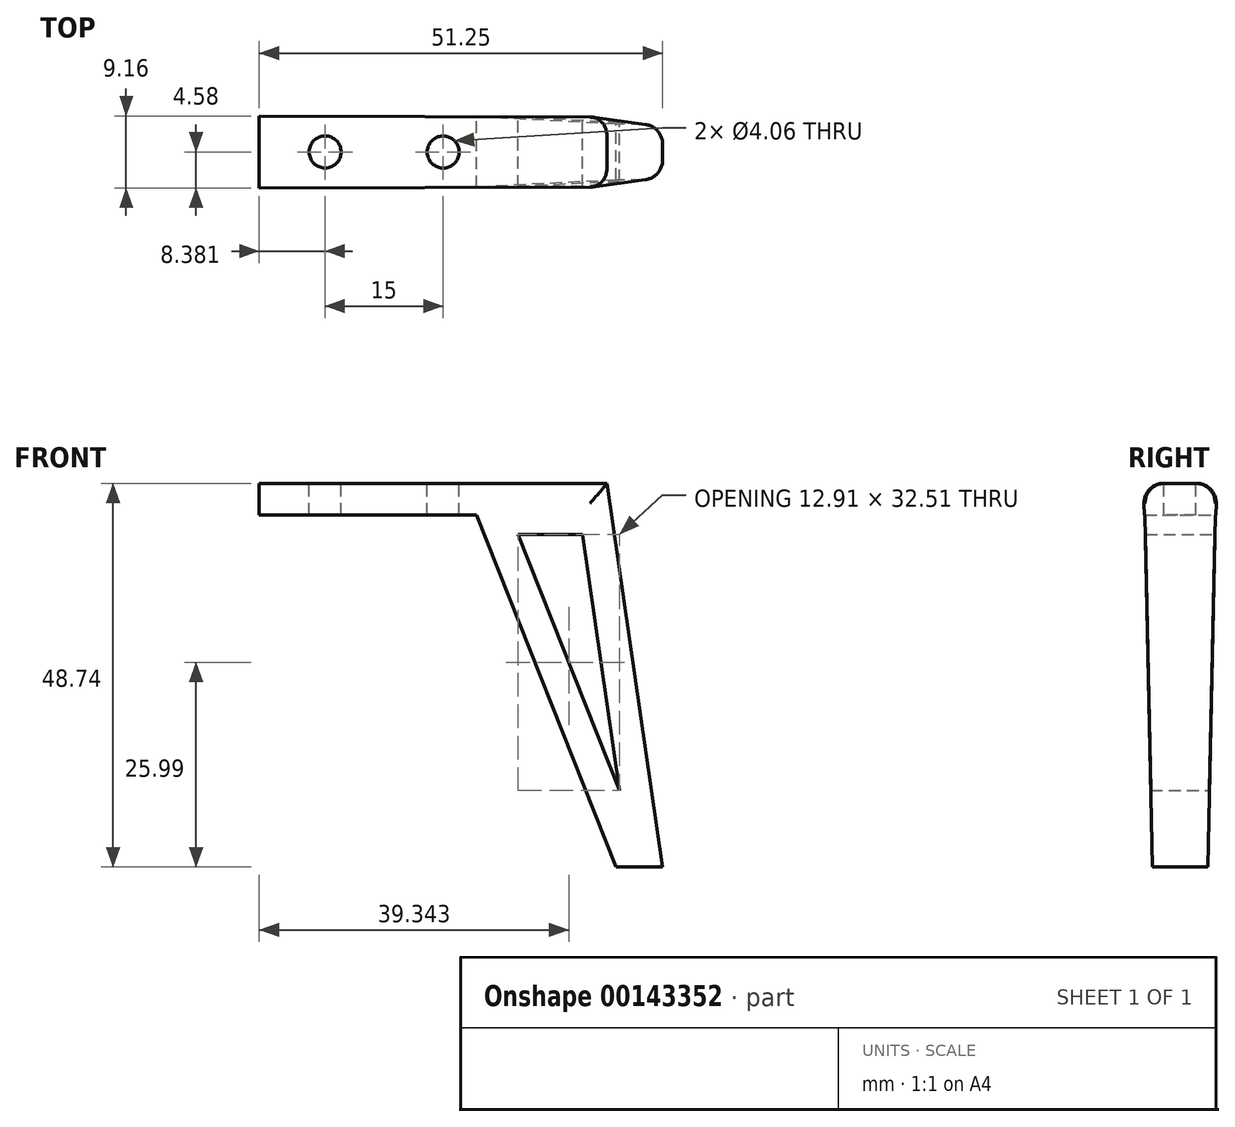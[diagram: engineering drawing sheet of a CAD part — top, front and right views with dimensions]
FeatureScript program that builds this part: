
annotation { "Feature Type Name" : "Feature", "Feature Type Description" : "" }
export const myFeature = defineFeature(function(context is Context, id is Id, definition is map)
    precondition{}
    {
        {
            var Q0;
            Q0=qCreatedBy(makeId("Front.planeOp"),FACE);
            var sketch = newSketch(context, id + "F0", { "sketchPlane" : qUnion([Q0])});
            skLineSegment(sketch, "E0.bottom", {"start": v(-26.8, -2) * mm, "end": v(0.8, -2) * mm});
            skLineSegment(sketch, "E0.top", {"start": v(-26.8, 2) * mm, "end": v(17.39, 2) * mm});
            skLineSegment(sketch, "E0.left", {"start": v(-26.8, -2) * mm, "end": v(-26.8, 2) * mm});
            skPoint(sketch, "E0.middle", {"position": v(0, 0) * mm});
            skLineSegment(sketch, "E1", {"start": v(0, 0) * mm, "end": v(18.56, -46.74) * mm});
            skLineSegment(sketch, "E2", {"start": v(18.56, -46.74) * mm, "end": v(24.45, -46.74) * mm});
            skLineSegment(sketch, "E3", {"start": v(17.39, 2) * mm, "end": v(24.45, -46.74) * mm});
            skPoint(sketch, "E4.orphan", {"position": v(26.8, 2) * mm});
            skPoint(sketch, "E5.orphan", {"position": v(26.8, -2) * mm});
            skLineSegment(sketch, "E6.0", {"start": v(6.09, -4.5) * mm, "end": v(19, -37) * mm});
            skLineSegment(sketch, "E7.0", {"start": v(14.29, -4.5) * mm, "end": v(19, -37) * mm});
            skLineSegment(sketch, "E8", {"start": v(6.09, -4.5) * mm, "end": v(14.29, -4.5) * mm});
            skSolve(sketch);
        }
        {
            var Q0;
            Q0 = qSketchRegion(id + "F0", true);
            extrude(context, id + "F1", {"entities" : qUnion([Q0]), "depth" : 11.5 * mm, "hasSecondDirection" : true, "secondDirectionOppositeDirection" : true, "secondDirectionDepth" : 7.25 * mm});
        }
        {
            var Q0;
            Q0=makeQuery(id+"F1.opExtrude","SWEPT_FACE",FACE,{"disambiguationData":[OSD([sQuery(id+"F0.wireOp",EDGE,"E3")])]});
            cPlane(context, id + "F2", {"entities" : qUnion([Q0]), "cplaneType" : CPlaneType.OFFSET, "offset" : 1.5 * mm, "width" : 150 * mm, "height" : 150 * mm});
        }
        {
            var Q0;
            Q0=qCreatedBy(id+"F2.planeOp",FACE);
            var sketch = newSketch(context, id + "F3", { "sketchPlane" : qUnion([Q0])});
            skLineSegment(sketch, "E9", {"start": v(-17.18, -51.7) * mm, "end": v(-3.49, -51.82) * mm});
            skLineSegment(sketch, "E10.MirrorCS", {"start": v(17.18, -51.7) * mm, "end": v(3.49, -51.82) * mm});
            skLineSegment(sketch, "E11", {"start": v(-3.49, -51.82) * mm, "end": v(-4.72, 10.55) * mm});
            skLineSegment(sketch, "E12", {"start": v(-4.72, 10.55) * mm, "end": v(-18.6, 10.28) * mm});
            skLineSegment(sketch, "E13", {"start": v(-18.6, 10.28) * mm, "end": v(-17.18, -51.7) * mm});
            skLineSegment(sketch, "E14.MirrorCS", {"start": v(3.49, -51.82) * mm, "end": v(4.72, 10.55) * mm});
            skLineSegment(sketch, "E15.MirrorCS", {"start": v(4.72, 10.55) * mm, "end": v(18.6, 10.28) * mm});
            skLineSegment(sketch, "E16.MirrorCS", {"start": v(18.6, 10.28) * mm, "end": v(17.18, -51.7) * mm});
            skSolve(sketch);
        }
        {
            var Q0;
            Q0=makeQuery(id+"F3.imprint","IMPRINT",FACE,{"disambiguationData":[TD([[makeQuery(id+"F3.imprint","IMPRINT",EDGE,{"derivedFrom":sQuery(id+"F3.wireOp",EDGE,"TnA0PpF5-dN3h-Jc00-I28Z-ERWVzqy0urNH")}),1.0]])]});
            var Q1;
            Q1=makeQuery(id+"F3.imprint","IMPRINT",FACE,{"disambiguationData":[TD([[makeQuery(id+"F3.imprint","IMPRINT",EDGE,{"derivedFrom":sQuery(id+"F3.wireOp",EDGE,"81dc0e61-a533-4fef-84a6-d9a5de71d5ed0.MirrorCS")}),-1.0]])]});
            var Q2;
            Q2=makeQuery(id+"F3.imprint","IMPRINT",FACE,{"disambiguationData":[TD([[makeQuery(id+"F3.imprint","IMPRINT",EDGE,{"derivedFrom":sQuery(id+"F3.wireOp",EDGE,"E9")}),1.0]])]});
            var Q3;
            Q3=makeQuery(id+"F3.imprint","IMPRINT",FACE,{"disambiguationData":[TD([[makeQuery(id+"F3.imprint","IMPRINT",EDGE,{"derivedFrom":sQuery(id+"F3.wireOp",EDGE,"E10.MirrorCS")}),-1.0]])]});
            extrude(context, id + "F4", {"entities" : qUnion([Q0, Q1, Q2, Q3]), "operationType" : NewBodyOperationType.REMOVE, "oppositeDirection" : true, "depth" : 57.75 * mm});
        }
        {
            var Q0;
            Q0=makeQuery(id+"F1.opExtrude","SWEPT_FACE",FACE,{"disambiguationData":[OSD([sQuery(id+"F0.wireOp",EDGE,"E0.top")])]});
            var sketch = newSketch(context, id + "F5", { "sketchPlane" : qUnion([Q0])});
            skCircle(sketch, "E17", {"center": v(-3.42, 0) * mm, "radius": 2.03 * mm});
            skCircle(sketch, "E18", {"center": v(-18.42, 0) * mm, "radius": 2.03 * mm});
            skSolve(sketch);
        }
        {
            var Q0;
            Q0=makeQuery(id+"F5.imprint","IMPRINT",FACE,{"disambiguationData":[TD([[makeQuery(id+"F5.imprint","IMPRINT",EDGE,{"derivedFrom":sQuery(id+"F5.wireOp",EDGE,"E17")}),1.0]])]});
            var Q1;
            Q1=makeQuery(id+"F5.imprint","IMPRINT",FACE,{"disambiguationData":[TD([[makeQuery(id+"F5.imprint","IMPRINT",EDGE,{"derivedFrom":sQuery(id+"F5.wireOp",EDGE,"E18")}),1.0]])]});
            extrude(context, id + "F6", {"entities" : qUnion([Q0, Q1]), "operationType" : NewBodyOperationType.REMOVE, "oppositeDirection" : true, "depth" : 25 * mm});
        }
        {
            var Q0;
            Q0=makeQuery(id+"F4.boolean.opBoolean","INTERSECT",EDGE,{"derivedFrom":[makeQuery(id+"F1.opExtrude","SWEPT_FACE",FACE,{"disambiguationData":[OSD([sQuery(id+"F0.wireOp",EDGE,"E0.top")])]}),makeQuery(id+"F4.opExtrude","SWEPT_FACE",FACE,{"disambiguationData":[OSD([sQuery(id+"F3.wireOp",EDGE,"E11")])]})]});
            var Q1;
            Q1=makeQuery(id+"F4.boolean.opBoolean","INTERSECT",EDGE,{"derivedFrom":[makeQuery(id+"F1.opExtrude","SWEPT_FACE",FACE,{"disambiguationData":[OSD([sQuery(id+"F0.wireOp",EDGE,"E0.top")])]}),makeQuery(id+"F4.opExtrude","SWEPT_FACE",FACE,{"disambiguationData":[OSD([sQuery(id+"F3.wireOp",EDGE,"E14.MirrorCS")])]})]});
            var Q2;
            Q2=makeQuery(id+"F4.boolean.opBoolean","INTERSECT",EDGE,{"derivedFrom":[makeQuery(id+"F1.opExtrude","SWEPT_FACE",FACE,{"disambiguationData":[OSD([sQuery(id+"F0.wireOp",EDGE,"E3")])]}),makeQuery(id+"F4.opExtrude","SWEPT_FACE",FACE,{"disambiguationData":[OSD([sQuery(id+"F3.wireOp",EDGE,"E14.MirrorCS")])]})]});
            var Q3;
            Q3=makeQuery(id+"F4.boolean.opBoolean","INTERSECT",EDGE,{"derivedFrom":[makeQuery(id+"F1.opExtrude","SWEPT_FACE",FACE,{"disambiguationData":[OSD([sQuery(id+"F0.wireOp",EDGE,"E3")])]}),makeQuery(id+"F4.opExtrude","SWEPT_FACE",FACE,{"disambiguationData":[OSD([sQuery(id+"F3.wireOp",EDGE,"E11")])]})]});
            fillet(context, id + "F7", {"entities" : qUnion([Q0, Q1, Q2, Q3]), "radius" : 2.5 * mm, "tangentPropagation" : true, "allowEdgeOverflow" : false});
        }
    });
